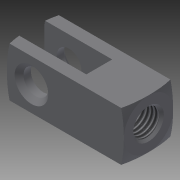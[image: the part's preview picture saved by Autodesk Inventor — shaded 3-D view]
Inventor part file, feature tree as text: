
AUTODESK INVENTOR PART (.ipt)
format: ipt  version: 2014 (Build 180170000, 170)  size: 201,216 bytes
history: native  units: in
note: dims shown in document units (in); Inventor stores cm internally (conversion verified against a paired STEP export)
features: other x126, sketch x7, revolve x3, extrude x2, hole x2
ambient origin geometry x8: Origin, YZ Plane, XZ Plane, XY Plane, X Axis, Y Axis, Z Axis, Center Point
bodies: Solid1 (feature_tree)
feature tree (140):
  extrude  "Extrusion1"  Depth=0.5in TaperAngle=0.0deg
  extrude  "Extrusion2"  TaperAngle=360.0deg  [1 undecoded]
  hole  "Hole1"  [1 undecoded]
  hole  "Hole2"  [1 undecoded]
  revolve  "Revolution1"  [1 undecoded]
  revolve  "Revolution2"  [1 undecoded]
  revolve  "Revolution3"  [1 undecoded]
  other  "dummy_XY"
  other  "dummy_YZ"
  other  "dummy_ZX"
  other  "dummy_X"
  other  "dummy_Y"
  other  "dummy_Z"
  other  "dummy_Center"
  other  "h1_XY"
  other  "h1_YZ"
  other  "h1_ZX"
  other  "h1_X"
  other  "h1_Y"
  other  "h1_Z"
  other  "h1_Center"
  other  "h2_XY"
  other  "h2_YZ"
  other  "h2_ZX"
  other  "h2_X"
  other  "h2_Y"
  other  "h2_Z"
  other  "h2_Center"
  other  "l1_XY"
  other  "l1_YZ"
  other  "l1_ZX"
  other  "l1_X"
  other  "l1_Y"
  other  "l1_Z"
  other  "l1_Center"
  other  "l11_XY"
  other  "l11_YZ"
  other  "l11_ZX"
  other  "l11_X"
  other  "l11_Y"
  other  "l11_Z"
  other  "l11_Center"
  other  "l12_XY"
  other  "l12_YZ"
  other  "l12_ZX"
  other  "l12_X"
  other  "l12_Y"
  other  "l12_Z"
  other  "l12_Center"
  other  "l2_XY"
  other  "l2_YZ"
  other  "l2_ZX"
  other  "l2_X"
  other  "l2_Y"
  other  "l2_Z"
  other  "l2_Center"
  other  "l21_XY"
  other  "l21_YZ"
  other  "l21_ZX"
  other  "l21_X"
  other  "l21_Y"
  other  "l21_Z"
  other  "l21_Center"
  other  "l22_XY"
  other  "l22_YZ"
  other  "l22_ZX"
  other  "l22_X"
  other  "l22_Y"
  other  "l22_Z"
  other  "l22_Center"
  other  "piston_rod_clevis_XY"
  other  "piston_rod_clevis_YZ"
  other  "piston_rod_clevis_ZX"
  other  "piston_rod_clevis_X"
  other  "piston_rod_clevis_Y"
  other  "piston_rod_clevis_Z"
  other  "piston_rod_clevis_Center"
  other  "rod_clevis_body_XY"
  other  "rod_clevis_body_YZ"
  other  "rod_clevis_body_ZX"
  other  "rod_clevis_body_X"
  other  "rod_clevis_body_Y"
  other  "rod_clevis_body_Z"
  other  "rod_clevis_body_Center"
  other  "th1_XY"
  other  "th1_YZ"
  other  "th1_ZX"
  other  "th1_X"
  other  "th1_Y"
  other  "th1_Z"
  other  "th1_Center"
  other  "th2_XY"
  other  "th2_YZ"
  other  "th2_ZX"
  other  "th2_X"
  other  "th2_Y"
  other  "th2_Z"
  other  "th2_Center"
  other  "to_cylinder_XY"
  other  "to_cylinder_YZ"
  other  "to_cylinder_ZX"
  other  "to_cylinder_X"
  other  "to_cylinder_Y"
  other  "to_cylinder_Z"
  other  "to_cylinder_Center"
  other  "w1_XY"
  other  "w1_YZ"
  other  "w1_ZX"
  other  "w1_X"
  other  "w1_Y"
  other  "w1_Z"
  other  "w1_Center"
  other  "w11_XY"
  other  "w11_YZ"
  other  "w11_ZX"
  other  "w11_X"
  other  "w11_Y"
  other  "w11_Z"
  other  "w11_Center"
  other  "w12_XY"
  other  "w12_YZ"
  other  "w12_ZX"
  other  "w12_X"
  other  "w12_Y"
  other  "w12_Z"
  other  "w12_Center"
  other  "w2_XY"
  other  "w2_YZ"
  other  "w2_ZX"
  other  "w2_X"
  other  "w2_Y"
  other  "w2_Z"
  other  "w2_Center"
  sketch  "Sketch_1"  dims[d0=0.5in d1=0.0in d2=0.5in d3=0.0in]
  sketch  "Sketch_2"  dims[d4=0.267in d5=0.44in d6=0.3125in d7=0.25in d8=90.0deg d9=0.44in d10=0.0in]
  sketch  "Sketch3"  dims[d11=0.2674in d12=0.75in d13=0.375in d14=0.25in d15=0.5635in d16=0.06in d17=0.0in d18=360.0deg]
  sketch  "Sketch4"  dims[d19=360.0deg d20=360.0deg]
  sketch  "Sketch_5"
  sketch  "Sketch_9"
  sketch  "Sketch_10"
note: 6 required parameter values undecoded (feature->parameter linkage not recoverable at this tier; creation-order binding heuristic only, values carry confidence <= 0.55)
